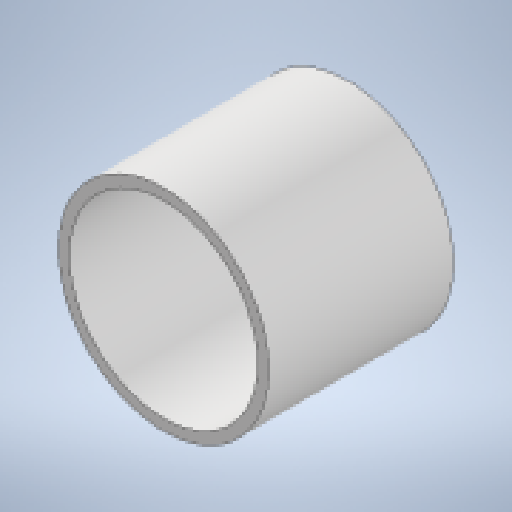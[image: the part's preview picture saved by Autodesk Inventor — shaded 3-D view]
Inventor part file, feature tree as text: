
AUTODESK INVENTOR PART (.ipt)
format: ipt  version: 2025.4 (Build 294407000, 407)  size: 146,944 bytes
history: native  units: mm
features: extrude x1, sketch x1
ambient origin geometry x8: Origin, YZ Plane, XZ Plane, XY Plane, X Axis, Y Axis, Z Axis, Center Point
bodies: Solid1 (feature_tree)
feature tree (2):
  extrude  "Extrusion1"  Depth=50.0mm
  sketch  "Sketch1"  dims[d0=57.0mm d1=3.0mm d2=50.0mm d3=0.0mm]
